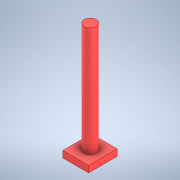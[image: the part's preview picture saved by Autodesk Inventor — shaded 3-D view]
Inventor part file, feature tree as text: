
AUTODESK INVENTOR PART (.ipt)
format: ipt  version: 2022 (Build 260153000, 153)  size: 99,328 bytes
history: imported  units: in
note: dims shown in document units (in); Inventor stores cm internally (conversion verified against a paired STEP export)
features: imported_body x1
ambient origin geometry x8: Origin, YZ Plane, XZ Plane, XY Plane, X Axis, Y Axis, Z Axis, Center Point
bodies: Solid1 (imported_parasolid), Body1 (imported_parasolid)
feature tree (1):
  imported_body  NMx_Import_Brep_tag  [imported B-rep: ~8 faces, bbox_mm=[47.0, 212.0, 52.0]]
